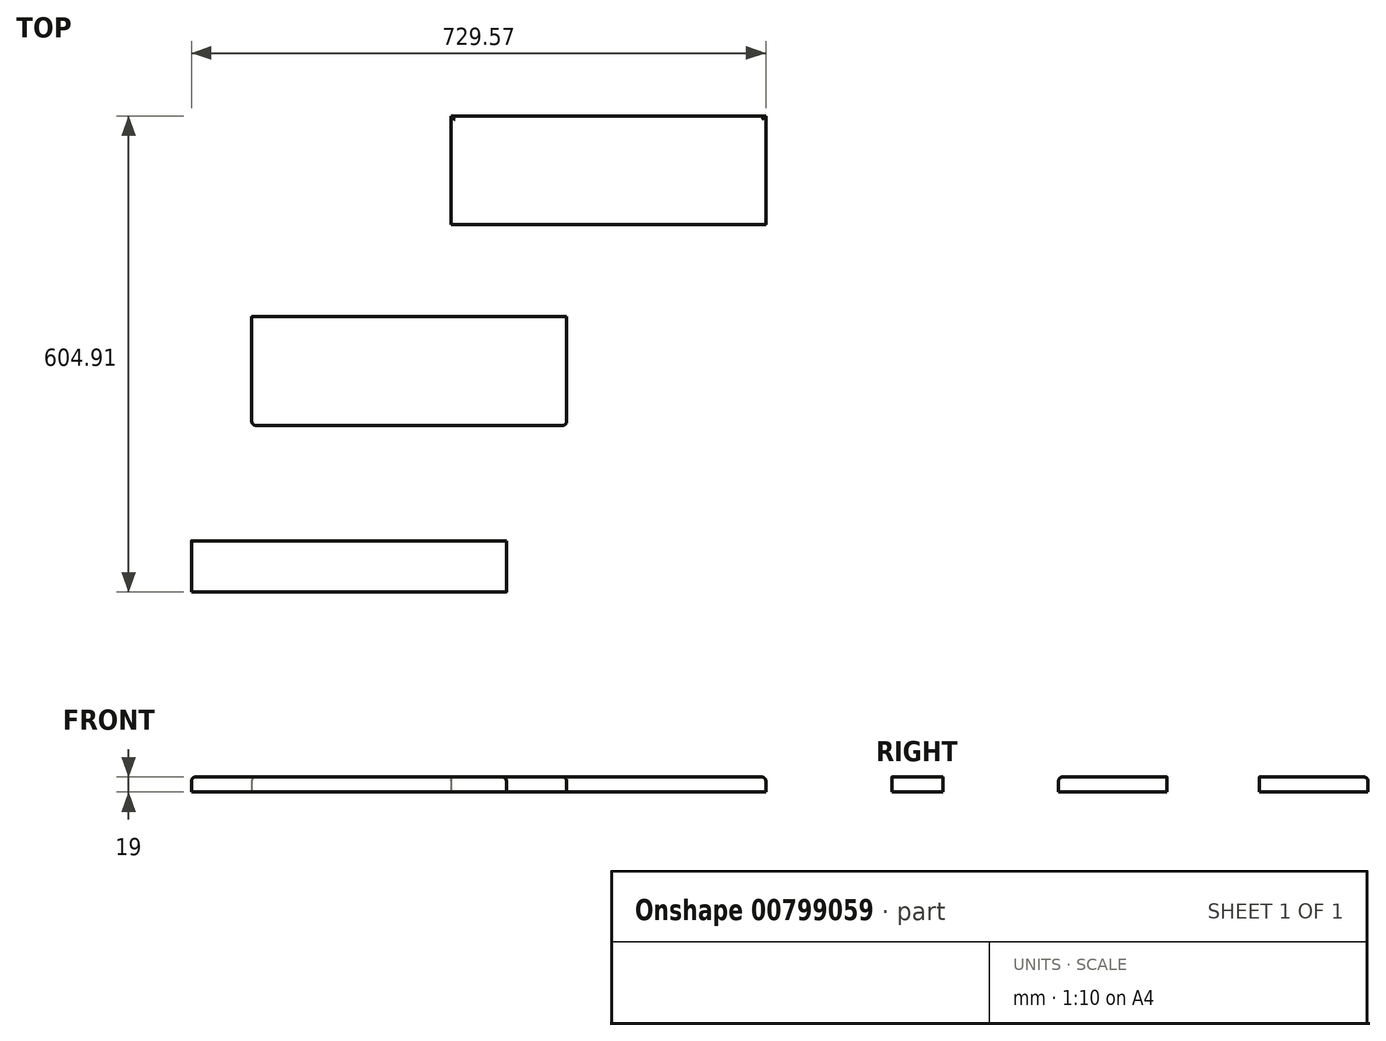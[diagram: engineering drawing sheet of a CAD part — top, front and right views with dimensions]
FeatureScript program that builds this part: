
annotation { "Feature Type Name" : "Feature", "Feature Type Description" : "" }
export const myFeature = defineFeature(function(context is Context, id is Id, definition is map)
    precondition{}
    {
        {
            var Q0;
            Q0=qCreatedBy(makeId("Top.planeOp"),FACE);
            var sketch = newSketch(context, id + "F0", { "sketchPlane" : qUnion([Q0])});
            skLineSegment(sketch, "E0.bottom", {"start": v(-492.74, 0) * mm, "end": v(-92.74, 0) * mm});
            skLineSegment(sketch, "E0.top", {"start": v(-492.74, -65) * mm, "end": v(-92.74, -65) * mm});
            skLineSegment(sketch, "E0.left", {"start": v(-492.74, 0) * mm, "end": v(-492.74, -65) * mm});
            skLineSegment(sketch, "E0.right", {"start": v(-92.74, 0) * mm, "end": v(-92.74, -65) * mm});
            skLineSegment(sketch, "E1.bottom", {"start": v(-416.11, 284.8) * mm, "end": v(-16.11, 284.8) * mm});
            skLineSegment(sketch, "E1.top", {"start": v(-416.11, 146.8) * mm, "end": v(-16.11, 146.8) * mm});
            skLineSegment(sketch, "E1.left", {"start": v(-416.11, 284.8) * mm, "end": v(-416.11, 146.8) * mm});
            skLineSegment(sketch, "E1.right", {"start": v(-16.11, 284.8) * mm, "end": v(-16.11, 146.8) * mm});
            skLineSegment(sketch, "E2.bottom", {"start": v(-163.17, 401.91) * mm, "end": v(236.83, 401.91) * mm});
            skLineSegment(sketch, "E2.top", {"start": v(-163.17, 539.91) * mm, "end": v(236.83, 539.91) * mm});
            skLineSegment(sketch, "E2.left", {"start": v(-163.17, 401.91) * mm, "end": v(-163.17, 539.91) * mm});
            skLineSegment(sketch, "E2.right", {"start": v(236.83, 401.91) * mm, "end": v(236.83, 539.91) * mm});
            skSolve(sketch);
        }
        {
            var Q0;
            Q0=makeQuery(id+"F0.imprint","IMPRINT",FACE,{"disambiguationData":[TD([[makeQuery(id+"F0.imprint","IMPRINT",EDGE,{"derivedFrom":sQuery(id+"F0.wireOp",EDGE,"E0.bottom")}),-1.0]])]});
            var Q1;
            Q1=makeQuery(id+"F0.imprint","IMPRINT",FACE,{"disambiguationData":[TD([[makeQuery(id+"F0.imprint","IMPRINT",EDGE,{"derivedFrom":sQuery(id+"F0.wireOp",EDGE,"E1.bottom")}),-1.0]])]});
            var Q2;
            Q2=makeQuery(id+"F0.imprint","IMPRINT",FACE,{"disambiguationData":[TD([[makeQuery(id+"F0.imprint","IMPRINT",EDGE,{"derivedFrom":sQuery(id+"F0.wireOp",EDGE,"E2.bottom")}),1.0]])]});
            extrude(context, id + "F1", {"entities" : qUnion([Q0, Q1, Q2]), "depth" : 19 * mm, "offsetDistance" : 25 * mm});
        }
        {
            var Q0;
            Q0=makeQuery(id+"F1.opExtrude","CAP_EDGE",EDGE,{"disambiguationData":[OSD([sQuery(id+"F0.wireOp",EDGE,"E1.top")])],"isStart":false});
            fillet(context, id + "F2", {"entities" : qUnion([Q0]), "radius" : 5 * mm, "tangentPropagation" : true, "allowEdgeOverflow" : false});
        }
        {
            var Q0;
            Q0=makeQuery(id+"F1.opExtrude","CAP_EDGE",EDGE,{"disambiguationData":[OSD([sQuery(id+"F0.wireOp",EDGE,"E1.right")])],"isStart":false});
            fillet(context, id + "F3", {"entities" : qUnion([Q0]), "radius" : 5 * mm, "tangentPropagation" : true, "allowEdgeOverflow" : false});
        }
        {
            var Q0;
            Q0=makeQuery(id+"F1.opExtrude","CAP_EDGE",EDGE,{"disambiguationData":[OSD([sQuery(id+"F0.wireOp",EDGE,"E1.left")])],"isStart":false});
            fillet(context, id + "F4", {"entities" : qUnion([Q0]), "radius" : 5 * mm, "tangentPropagation" : true, "allowEdgeOverflow" : false});
        }
        {
            var Q0;
            Q0=makeQuery(id+"F1.opExtrude","CAP_EDGE",EDGE,{"disambiguationData":[OSD([sQuery(id+"F0.wireOp",EDGE,"E0.left")])],"isStart":false});
            var Q1;
            Q1=makeQuery(id+"F1.opExtrude","CAP_EDGE",EDGE,{"disambiguationData":[OSD([sQuery(id+"F0.wireOp",EDGE,"E0.right")])],"isStart":false});
            fillet(context, id + "F5", {"entities" : qUnion([Q0, Q1]), "radius" : 5 * mm, "tangentPropagation" : true, "allowEdgeOverflow" : false});
        }
        {
            var Q0;
            Q0=makeQuery(id+"F1.opExtrude","CAP_EDGE",EDGE,{"disambiguationData":[OSD([sQuery(id+"F0.wireOp",EDGE,"E2.left")])],"isStart":false});
            var Q1;
            Q1=makeQuery(id+"F1.opExtrude","CAP_EDGE",EDGE,{"disambiguationData":[OSD([sQuery(id+"F0.wireOp",EDGE,"E2.top")])],"isStart":false});
            var Q2;
            Q2=makeQuery(id+"F1.opExtrude","CAP_EDGE",EDGE,{"disambiguationData":[OSD([sQuery(id+"F0.wireOp",EDGE,"E2.right")])],"isStart":false});
            fillet(context, id + "F6", {"entities" : qUnion([Q0, Q1, Q2]), "radius" : 5 * mm, "tangentPropagation" : true, "allowEdgeOverflow" : false});
        }
    });
